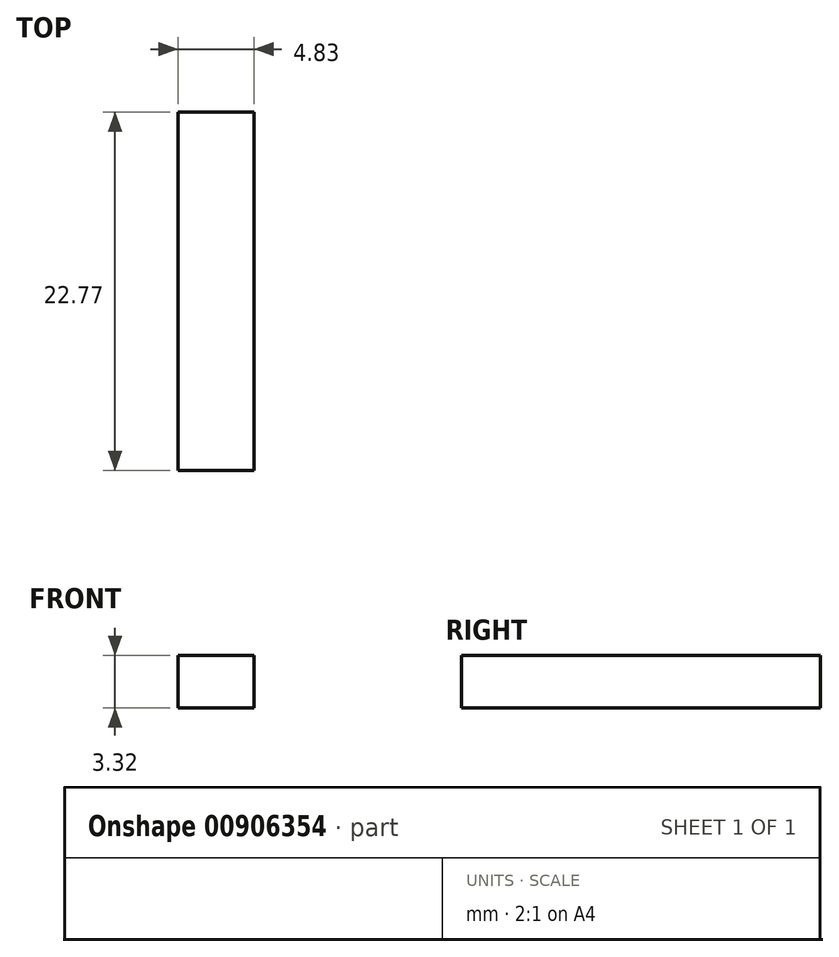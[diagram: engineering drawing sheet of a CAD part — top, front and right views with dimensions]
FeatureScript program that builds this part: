
annotation { "Feature Type Name" : "Feature", "Feature Type Description" : "" }
export const myFeature = defineFeature(function(context is Context, id is Id, definition is map)
    precondition{}
    {
        {
            var Q0;
            Q0=qCreatedBy(makeId("Top.planeOp"),FACE);
            var sketch = newSketch(context, id + "F0", { "sketchPlane" : qUnion([Q0])});
            skLineSegment(sketch, "E0.bottom", {"start": v(-10.5, 40.74) * mm, "end": v(-15.34, 40.74) * mm});
            skLineSegment(sketch, "E0.top", {"start": v(-10.5, 17.97) * mm, "end": v(-15.34, 17.97) * mm});
            skLineSegment(sketch, "E0.left", {"start": v(-10.5, 40.74) * mm, "end": v(-10.5, 17.97) * mm});
            skLineSegment(sketch, "E0.right", {"start": v(-15.34, 40.74) * mm, "end": v(-15.34, 17.97) * mm});
            skSolve(sketch);
        }
        {
            var Q0;
            Q0=makeQuery(id+"F0.imprint","IMPRINT",FACE,{"disambiguationData":[TD([[makeQuery(id+"F0.imprint","IMPRINT",EDGE,{"derivedFrom":sQuery(id+"F0.wireOp",EDGE,"E0.bottom")}),1.0]])]});
            extrude(context, id + "F1", {"entities" : qUnion([Q0]), "depth" : 3.32 * mm, "offsetDistance" : 25.4 * mm});
        }
    });
